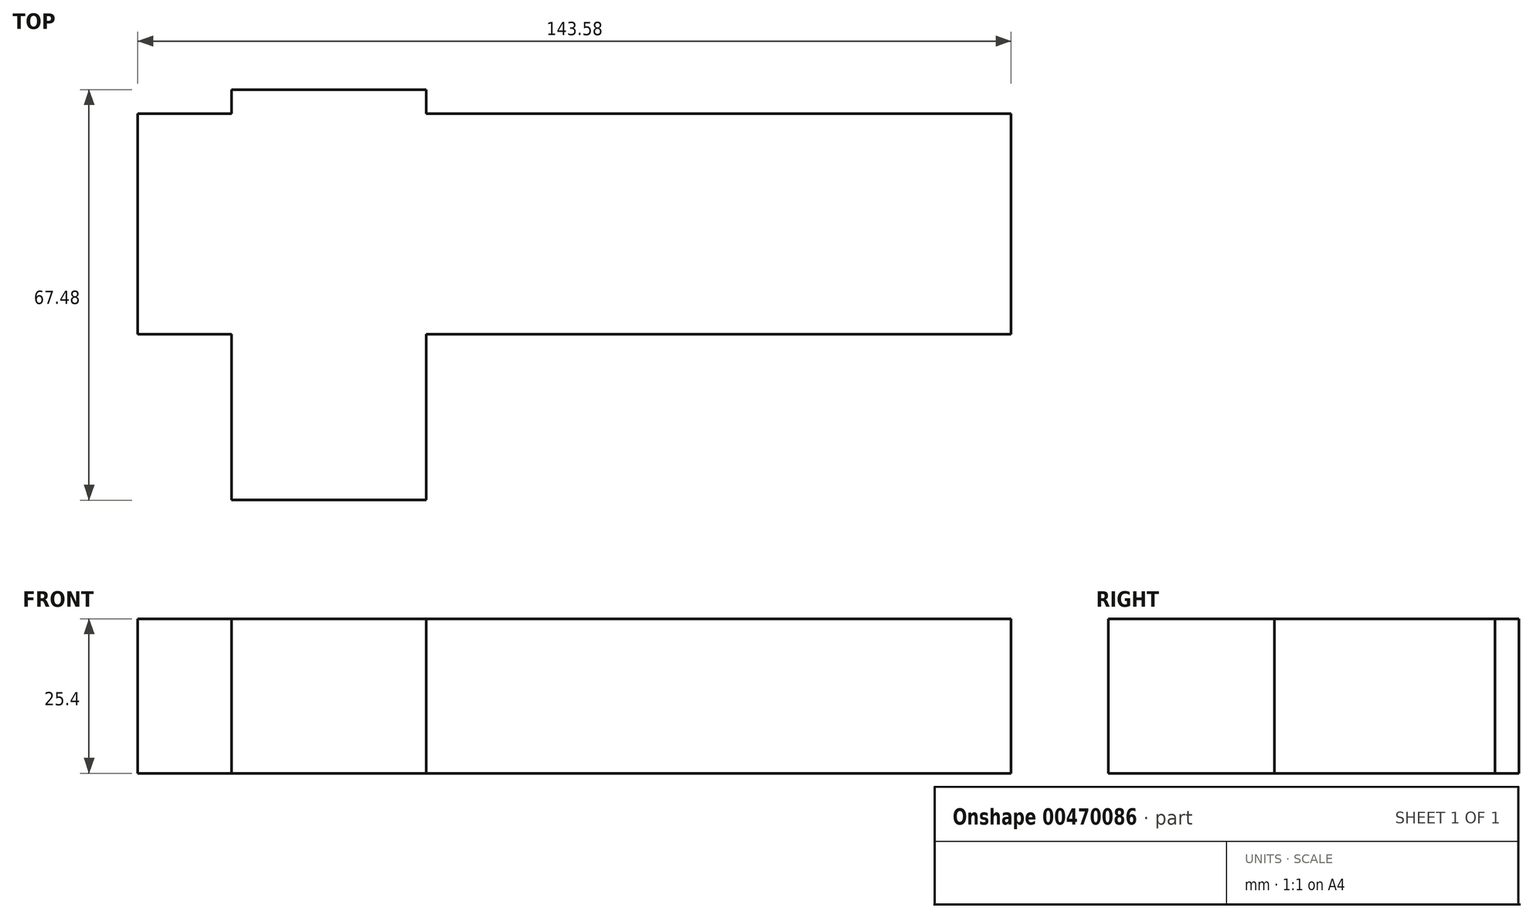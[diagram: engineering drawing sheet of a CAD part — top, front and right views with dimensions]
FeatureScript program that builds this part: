
annotation { "Feature Type Name" : "Feature", "Feature Type Description" : "" }
export const myFeature = defineFeature(function(context is Context, id is Id, definition is map)
    precondition{}
    {
        {
            var Q0;
            Q0=qCreatedBy(makeId("Top.planeOp"),FACE);
            var sketch = newSketch(context, id + "F0", { "sketchPlane" : qUnion([Q0])});
            skLineSegment(sketch, "E0.bottom", {"start": v(-24.69, -33.74) * mm, "end": v(-56.68, -33.74) * mm});
            skLineSegment(sketch, "E0.top", {"start": v(-24.69, 33.74) * mm, "end": v(-56.68, 33.74) * mm});
            skLineSegment(sketch, "E0.left", {"start": v(-24.69, -33.74) * mm, "end": v(-24.69, 33.74) * mm});
            skLineSegment(sketch, "E0.right", {"start": v(-56.68, -33.74) * mm, "end": v(-56.68, 33.74) * mm});
            skPoint(sketch, "E0.middle", {"position": v(-40.69, 0) * mm});
            skLineSegment(sketch, "E1.bottom", {"start": v(71.47, 29.8) * mm, "end": v(-72.1, 29.8) * mm});
            skLineSegment(sketch, "E1.top", {"start": v(71.47, -6.46) * mm, "end": v(-72.1, -6.46) * mm});
            skLineSegment(sketch, "E1.left", {"start": v(71.47, 29.8) * mm, "end": v(71.47, -6.46) * mm});
            skLineSegment(sketch, "E1.right", {"start": v(-72.1, 29.8) * mm, "end": v(-72.1, -6.46) * mm});
            skPoint(sketch, "E1.middle", {"position": v(-0.32, 11.66) * mm});
            skLineSegment(sketch, "E2.bottom", {"start": v(82.77, 131.2) * mm, "end": v(39.81, 131.2) * mm, "construction": true});
            skLineSegment(sketch, "E2.top", {"start": v(82.77, 58.2) * mm, "end": v(39.81, 58.2) * mm, "construction": true});
            skLineSegment(sketch, "E2.left", {"start": v(82.77, 131.2) * mm, "end": v(82.77, 58.2) * mm, "construction": true});
            skLineSegment(sketch, "E2.right", {"start": v(39.81, 131.2) * mm, "end": v(39.81, 58.2) * mm, "construction": true});
            skPoint(sketch, "E2.middle", {"position": v(61.3, 94.7) * mm});
            skSolve(sketch);
        }
        {
            var Q0;
            Q0 = qSketchRegion(id + "F0", true);
            extrude(context, id + "F1", {"entities" : qUnion([Q0]), "depth" : 25.4 * mm});
        }
    });
